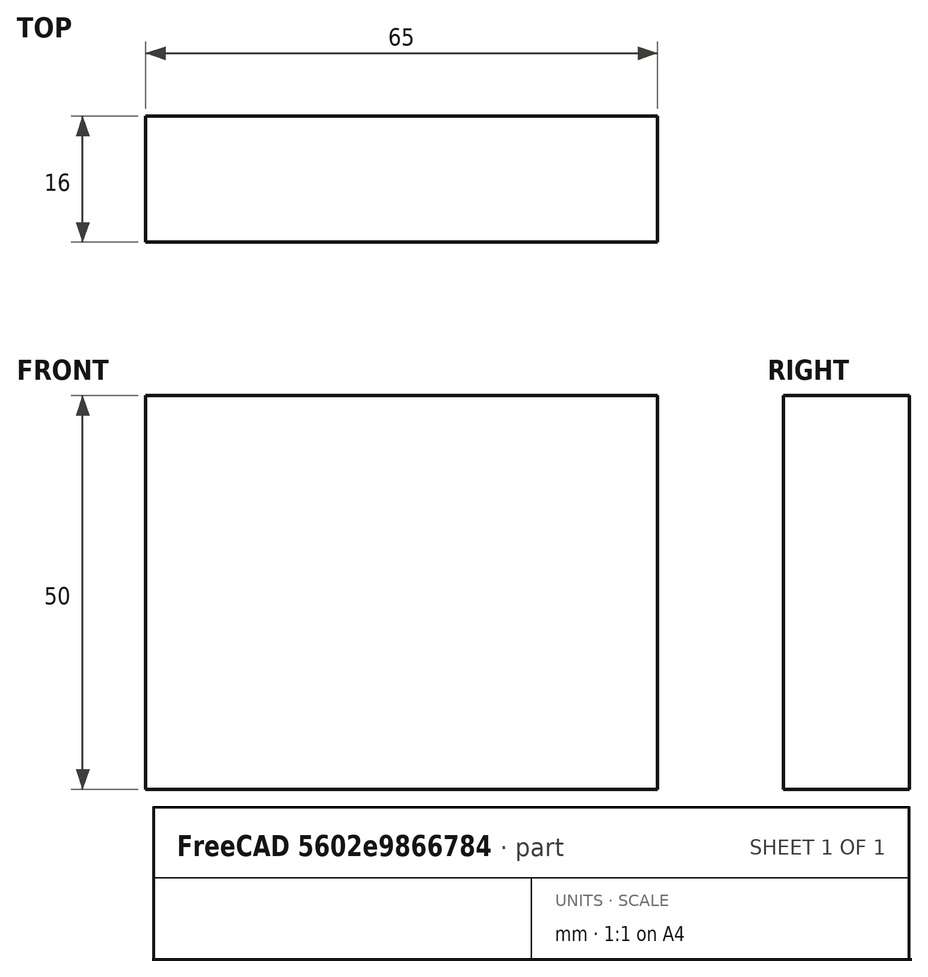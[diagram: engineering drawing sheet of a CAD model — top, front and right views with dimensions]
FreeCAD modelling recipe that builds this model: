
FCSTD DOCUMENT  (FreeCAD 0.15R4671 (Git))
Label: Flat Bar 65x16 EN10058 S235JR
License: All rights reserved
LicenseURL: http://en.wikipedia.org/wiki/All_rights_reserved
objects: Sketcher::SketchObject×1, Part::Extrusion×1
note: 2 computed .brp shape members not serialized (recipe doc carries the construction recipe); baked Part::Feature solids carry a one-line shape summary decoded from their .brp

FEATURE [Sketcher::SketchObject] Sketch
  sketch-geometry (4):
    g0: LineSegment StartX=-32.5 StartY=-8 StartZ=0 EndX=32.5 EndY=-8 EndZ=0
    g1: LineSegment StartX=32.5 StartY=-8 StartZ=0 EndX=32.5 EndY=8 EndZ=0
    g2: LineSegment StartX=32.5 StartY=8 StartZ=0 EndX=-32.5 EndY=8 EndZ=0
    g3: LineSegment StartX=-32.5 StartY=8 StartZ=0 EndX=-32.5 EndY=-8 EndZ=0
  constraints (12):
    c: Coincident(g0,g1)
    c: Coincident(g1,g2)
    c: Coincident(g2,g3)
    c: Coincident(g3,g0)
    c: Horizontal(g0)
    c: Horizontal(g2)
    c: Vertical(g1)
    c: Vertical(g3)
    c: Symmetric(g1,g2,g-2)
    c: Symmetric(g0,g1,g-1)
    c: DistanceY(g1) = 16
    c: DistanceX(g0) = 65
FEATURE [Part::Extrusion] Extrude  label="Flat Bar 65x16 EN10058 S235JR"
  Base = -> Sketch
  Dir = (0,0,50)
  Solid = true
